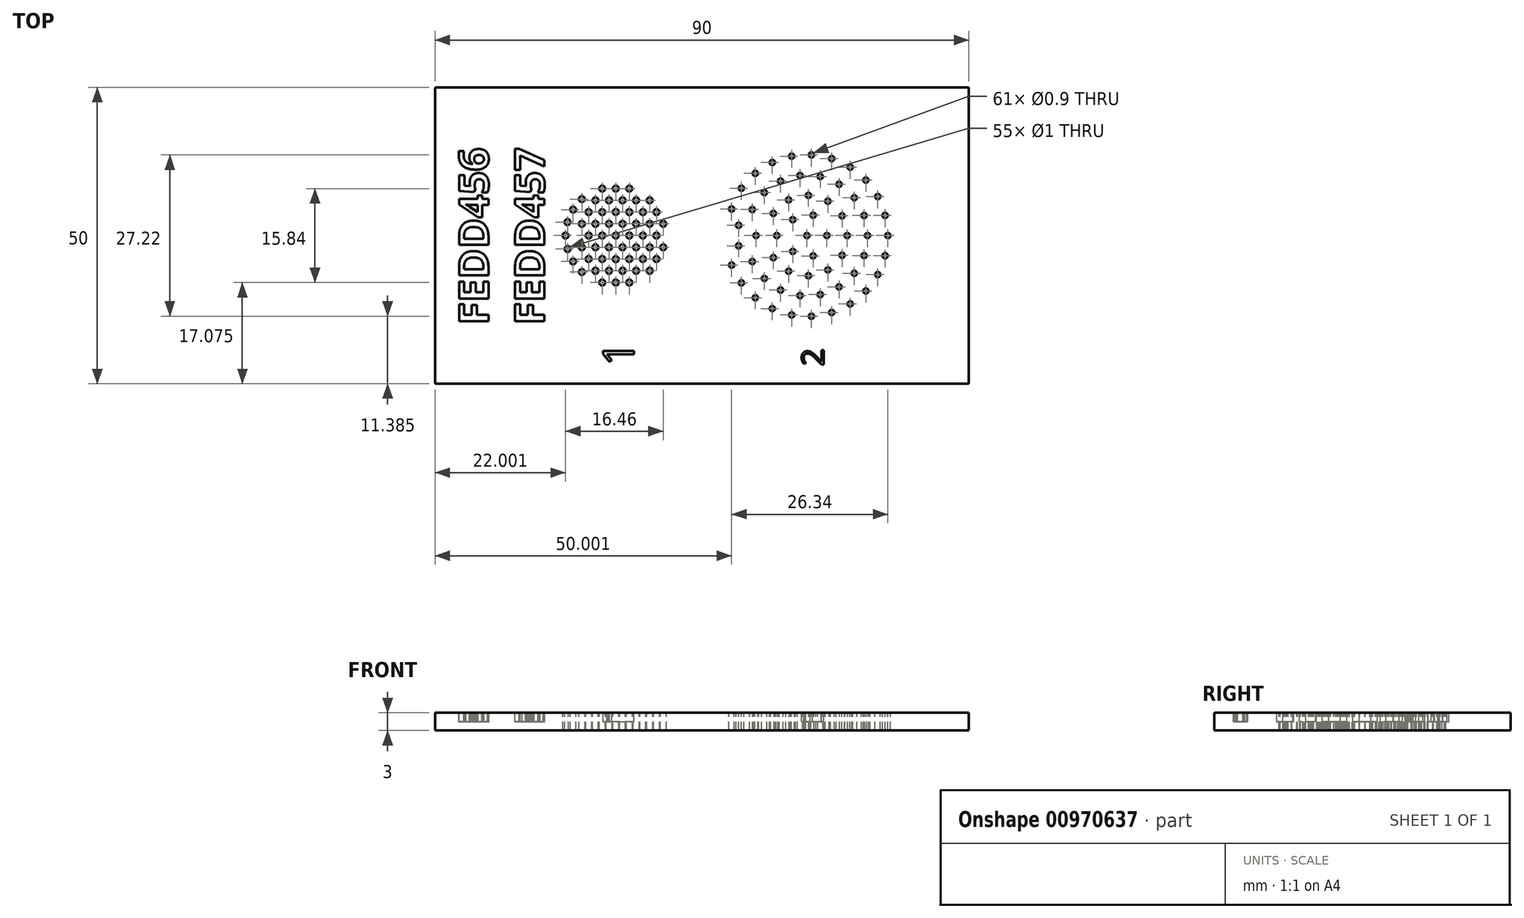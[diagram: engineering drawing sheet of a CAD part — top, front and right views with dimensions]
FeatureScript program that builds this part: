
annotation { "Feature Type Name" : "Feature", "Feature Type Description" : "" }
export const myFeature = defineFeature(function(context is Context, id is Id, definition is map)
    precondition{}
    {
        {
            var Q0;
            Q0=qCreatedBy(makeId("Top.planeOp"),FACE);
            var sketch = newSketch(context, id + "F0", { "sketchPlane" : qUnion([Q0])});
            skLineSegment(sketch, "E0.bottom", {"start": v(-43.16, 28.34) * mm, "end": v(46.84, 28.34) * mm});
            skLineSegment(sketch, "E0.top", {"start": v(-43.16, -21.66) * mm, "end": v(46.84, -21.66) * mm});
            skLineSegment(sketch, "E0.left", {"start": v(-43.16, 28.34) * mm, "end": v(-43.16, -21.66) * mm});
            skLineSegment(sketch, "E0.right", {"start": v(46.84, 28.34) * mm, "end": v(46.84, -21.66) * mm});
            skSolve(sketch);
        }
        {
            var Q0;
            Q0=makeQuery(id+"F0.imprint","IMPRINT",FACE,{"disambiguationData":[TD([[makeQuery(id+"F0.imprint","IMPRINT",EDGE,{"derivedFrom":sQuery(id+"F0.wireOp",EDGE,"E0.bottom")}),-1.0]])]});
            extrude(context, id + "F1", {"entities" : qUnion([Q0]), "depth" : 3 * mm, "offsetDistance" : 25 * mm});
        }
        {
            var Q0;
            Q0=makeQuery(id+"F1.opExtrude","CAP_FACE",FACE,{"disambiguationData":[OSD([sQuery(id+"F0.wireOp",EDGE,"E0.bottom"),sQuery(id+"F0.wireOp",EDGE,"E0.top"),sQuery(id+"F0.wireOp",EDGE,"E0.left"),sQuery(id+"F0.wireOp",EDGE,"E0.right")])],"isStart":false});
            var sketch = newSketch(context, id + "F2", { "sketchPlane" : qUnion([Q0])});
            skText(sketch, "E1", { "text": "FEDD456 \nFEDD457", "fontName": "OpenSans-Bold.ttf"});
            skText(sketch, "E2", { "text": "1", "fontName": "OpenSans-Regular.ttf"});
            skText(sketch, "E3", { "text": "2", "fontName": "OpenSans-Regular.ttf"});
            const initialGuessF2  = {"E1": [-0.03416, -0.01171, 0, 1, 0.005], "E2": [-0.00966, -0.01866, 0, 1, 0.00522], "E3": [0.02236, -0.01866, 0, 1, 0.0037]};
            skSetInitialGuess(sketch, initialGuessF2);
            skSolve(sketch);
        }
        {
            var Q0;
            Q0=qSketchRegion(id+"F2",true);
            extrude(context, id + "F3", {"entities" : qUnion([Q0]), "operationType" : NewBodyOperationType.REMOVE, "oppositeDirection" : true, "depth" : 1.5 * mm, "offsetDistance" : 25 * mm});
        }
        {
            var Q0;
            {var subQ0=sQuery(id+"F0.wireOp",EDGE,"E0.left");var subQ1=sQuery(id+"F0.wireOp",EDGE,"E0.bottom");var subQ2=sQuery(id+"F0.wireOp",EDGE,"E0.right");var subQ3=sQuery(id+"F0.wireOp",EDGE,"E0.top");Q0=makeQuery(id+"F3.boolean.opBoolean","SPLIT",FACE,{"disambiguationData":[TD([makeQuery(id+"F1.opExtrude","SWEPT_FACE",FACE,{"disambiguationData":[OSD([subQ1])]})])],"derivedFrom":makeQuery(id+"F1.opExtrude","CAP_FACE",FACE,{"disambiguationData":[OSD([subQ1,subQ3,subQ0,subQ2])],"isStart":false})});}
            var sketch = newSketch(context, id + "F4", { "sketchPlane" : qUnion([Q0])});
            skLineSegment(sketch, "E4", {"start": v(-27.8, 3.34) * mm, "end": v(2.56, 3.34) * mm});
            skLineSegment(sketch, "E5", {"start": v(-12.8, -15.66) * mm, "end": v(-12.8, 21.7) * mm});
            skCircle(sketch, "E6", {"center": v(-14.98, -4.58) * mm, "radius": 0.5 * mm});
            skCircle(sketch, "E7", {"center": v(-18.4, -2.81) * mm, "radius": 0.5 * mm});
            skCircle(sketch, "E8", {"center": v(-19.89, -1.03) * mm, "radius": 0.5 * mm});
            skCircle(sketch, "E9", {"center": v(-20.83, 1.08) * mm, "radius": 0.5 * mm});
            skCircle(sketch, "E10", {"center": v(-21.16, 3.34) * mm, "radius": 0.5 * mm});
            skCircle(sketch, "E11", {"center": v(-20.83, 5.6) * mm, "radius": 0.5 * mm});
            skCircle(sketch, "E12", {"center": v(-19.89, 7.7) * mm, "radius": 0.5 * mm});
            skCircle(sketch, "E13", {"center": v(-18.4, 9.49) * mm, "radius": 0.5 * mm});
            skCircle(sketch, "E14", {"center": v(-14.98, 11.26) * mm, "radius": 0.5 * mm});
            skCircle(sketch, "E15", {"center": v(-10.4, 11.26) * mm, "radius": 0.5 * mm});
            skCircle(sketch, "E16", {"center": v(-6.98, 9.28) * mm, "radius": 0.5 * mm});
            skCircle(sketch, "E17", {"center": v(-5.84, 7.3) * mm, "radius": 0.5 * mm});
            skCircle(sketch, "E18", {"center": v(-4.7, 5.32) * mm, "radius": 0.5 * mm});
            skCircle(sketch, "E19", {"center": v(-4.7, 1.36) * mm, "radius": 0.5 * mm});
            skCircle(sketch, "E20", {"center": v(-5.84, -0.62) * mm, "radius": 0.5 * mm});
            skCircle(sketch, "E21", {"center": v(-6.98, -2.6) * mm, "radius": 0.5 * mm});
            skCircle(sketch, "E22", {"center": v(-10.4, -4.58) * mm, "radius": 0.5 * mm});
            skCircle(sketch, "E23", {"center": v(-12.7, -4.58) * mm, "radius": 0.5 * mm});
            skCircle(sketch, "E24", {"center": v(-18.4, 5.32) * mm, "radius": 0.5 * mm});
            skCircle(sketch, "E25", {"center": v(-17.27, 7.3) * mm, "radius": 0.5 * mm});
            skCircle(sketch, "E26", {"center": v(-16.13, 9.28) * mm, "radius": 0.5 * mm});
            skCircle(sketch, "E27", {"center": v(-13.84, 9.28) * mm, "radius": 0.5 * mm});
            skCircle(sketch, "E28", {"center": v(-16.13, 5.32) * mm, "radius": 0.5 * mm});
            skCircle(sketch, "E29", {"center": v(-14.98, 7.3) * mm, "radius": 0.5 * mm});
            skCircle(sketch, "E30", {"center": v(-13.84, 5.32) * mm, "radius": 0.5 * mm});
            skCircle(sketch, "E31", {"center": v(-12.7, 11.26) * mm, "radius": 0.5 * mm});
            skCircle(sketch, "E32", {"center": v(-9.27, 9.28) * mm, "radius": 0.5 * mm});
            skCircle(sketch, "E33", {"center": v(-8.13, 7.3) * mm, "radius": 0.5 * mm});
            skCircle(sketch, "E34", {"center": v(-9.27, 5.32) * mm, "radius": 0.5 * mm});
            skCircle(sketch, "E35", {"center": v(-10.4, 7.3) * mm, "radius": 0.5 * mm});
            skCircle(sketch, "E36", {"center": v(-11.56, 5.32) * mm, "radius": 0.5 * mm});
            skCircle(sketch, "E37", {"center": v(-12.7, 7.32) * mm, "radius": 0.5 * mm});
            skCircle(sketch, "E38", {"center": v(-17.27, 3.34) * mm, "radius": 0.5 * mm});
            skCircle(sketch, "E39", {"center": v(-14.98, 3.34) * mm, "radius": 0.5 * mm});
            skCircle(sketch, "E40", {"center": v(-12.7, 3.34) * mm, "radius": 0.5 * mm});
            skCircle(sketch, "E41", {"center": v(-10.4, 3.34) * mm, "radius": 0.5 * mm});
            skCircle(sketch, "E42", {"center": v(-8.13, 3.34) * mm, "radius": 0.5 * mm});
            skCircle(sketch, "E43", {"center": v(-5.84, 3.34) * mm, "radius": 0.5 * mm});
            skCircle(sketch, "E44", {"center": v(-18.4, 1.36) * mm, "radius": 0.5 * mm});
            skCircle(sketch, "E45", {"center": v(-16.13, 1.36) * mm, "radius": 0.5 * mm});
            skCircle(sketch, "E46", {"center": v(-13.84, 1.36) * mm, "radius": 0.5 * mm});
            skCircle(sketch, "E47", {"center": v(-11.56, 1.36) * mm, "radius": 0.5 * mm});
            skCircle(sketch, "E48", {"center": v(-9.27, 1.36) * mm, "radius": 0.5 * mm});
            skCircle(sketch, "E49", {"center": v(-6.98, 1.36) * mm, "radius": 0.5 * mm});
            skCircle(sketch, "E50", {"center": v(-17.27, -0.62) * mm, "radius": 0.5 * mm});
            skCircle(sketch, "E51", {"center": v(-14.98, -0.62) * mm, "radius": 0.5 * mm});
            skCircle(sketch, "E52", {"center": v(-12.7, -0.64) * mm, "radius": 0.5 * mm});
            skCircle(sketch, "E53", {"center": v(-10.4, -0.62) * mm, "radius": 0.5 * mm});
            skCircle(sketch, "E54", {"center": v(-8.13, -0.62) * mm, "radius": 0.5 * mm});
            skCircle(sketch, "E55", {"center": v(-16.13, -2.6) * mm, "radius": 0.5 * mm});
            skCircle(sketch, "E56", {"center": v(-13.84, -2.6) * mm, "radius": 0.5 * mm});
            skCircle(sketch, "E57", {"center": v(-11.56, -2.6) * mm, "radius": 0.5 * mm});
            skCircle(sketch, "E58", {"center": v(-9.27, -2.6) * mm, "radius": 0.5 * mm});
            skCircle(sketch, "E59", {"center": v(-6.98, 5.32) * mm, "radius": 0.5 * mm});
            skCircle(sketch, "E60", {"center": v(-11.56, 9.28) * mm, "radius": 0.5 * mm});
            skLineSegment(sketch, "E61", {"start": v(4.04, 3.34) * mm, "end": v(37.05, 3.34) * mm});
            skLineSegment(sketch, "E62", {"start": v(19.54, -13.72) * mm, "end": v(19.54, 21.34) * mm});
            skCircle(sketch, "E63", {"center": v(6.84, 7.82) * mm, "radius": 0.45 * mm});
            skCircle(sketch, "E64", {"center": v(8.5, 11.32) * mm, "radius": 0.45 * mm});
            skCircle(sketch, "E65", {"center": v(10.83, 13.83) * mm, "radius": 0.45 * mm});
            skCircle(sketch, "E66", {"center": v(13.7, 15.66) * mm, "radius": 0.45 * mm});
            skCircle(sketch, "E67", {"center": v(16.97, 16.73) * mm, "radius": 0.45 * mm});
            skCircle(sketch, "E68", {"center": v(20.3, 16.95) * mm, "radius": 0.45 * mm});
            skCircle(sketch, "E69", {"center": v(23.71, 16.32) * mm, "radius": 0.45 * mm});
            skCircle(sketch, "E70", {"center": v(26.83, 14.87) * mm, "radius": 0.45 * mm});
            skCircle(sketch, "E71", {"center": v(29.47, 12.69) * mm, "radius": 0.45 * mm});
            skCircle(sketch, "E72", {"center": v(31.48, 9.92) * mm, "radius": 0.45 * mm});
            skCircle(sketch, "E73", {"center": v(32.72, 6.74) * mm, "radius": 0.45 * mm});
            skCircle(sketch, "E74", {"center": v(32.72, -0.06) * mm, "radius": 0.45 * mm});
            skCircle(sketch, "E75", {"center": v(31.48, -3.24) * mm, "radius": 0.45 * mm});
            skCircle(sketch, "E76", {"center": v(29.47, -6.01) * mm, "radius": 0.45 * mm});
            skCircle(sketch, "E77", {"center": v(26.83, -8.2) * mm, "radius": 0.45 * mm});
            skCircle(sketch, "E78", {"center": v(23.71, -9.64) * mm, "radius": 0.45 * mm});
            skCircle(sketch, "E79", {"center": v(20.3, -10.27) * mm, "radius": 0.45 * mm});
            skCircle(sketch, "E80", {"center": v(16.97, -10.05) * mm, "radius": 0.45 * mm});
            skCircle(sketch, "E81", {"center": v(13.7, -8.98) * mm, "radius": 0.45 * mm});
            skCircle(sketch, "E82", {"center": v(10.83, -7.15) * mm, "radius": 0.45 * mm});
            skCircle(sketch, "E83", {"center": v(8.5, -4.64) * mm, "radius": 0.45 * mm});
            skCircle(sketch, "E84", {"center": v(6.84, -1.64) * mm, "radius": 0.45 * mm});
            skCircle(sketch, "E85", {"center": v(8.01, 5.07) * mm, "radius": 0.45 * mm});
            skCircle(sketch, "E86", {"center": v(10.32, 7.73) * mm, "radius": 0.45 * mm});
            skCircle(sketch, "E87", {"center": v(12.35, 10.58) * mm, "radius": 0.45 * mm});
            skCircle(sketch, "E88", {"center": v(15.1, 12.53) * mm, "radius": 0.45 * mm});
            skCircle(sketch, "E89", {"center": v(18.37, 13.47) * mm, "radius": 0.45 * mm});
            skCircle(sketch, "E90", {"center": v(21.78, 13.3) * mm, "radius": 0.45 * mm});
            skCircle(sketch, "E91", {"center": v(24.95, 12) * mm, "radius": 0.45 * mm});
            skCircle(sketch, "E92", {"center": v(27.52, 9.72) * mm, "radius": 0.45 * mm});
            skCircle(sketch, "E93", {"center": v(19.8, 10.12) * mm, "radius": 0.45 * mm});
            skCircle(sketch, "E94", {"center": v(23.07, 9.13) * mm, "radius": 0.45 * mm});
            skCircle(sketch, "E95", {"center": v(25.46, 6.67) * mm, "radius": 0.45 * mm});
            skCircle(sketch, "E96", {"center": v(20.58, 6.77) * mm, "radius": 0.45 * mm});
            skCircle(sketch, "E97", {"center": v(13.88, 7.07) * mm, "radius": 0.45 * mm});
            skCircle(sketch, "E98", {"center": v(16.44, 9.36) * mm, "radius": 0.45 * mm});
            skCircle(sketch, "E99", {"center": v(17.15, 6) * mm, "radius": 0.45 * mm});
            skCircle(sketch, "E100", {"center": v(8.01, 1.6) * mm, "radius": 0.45 * mm});
            skCircle(sketch, "E101", {"center": v(10.32, -1.05) * mm, "radius": 0.45 * mm});
            skCircle(sketch, "E102", {"center": v(12.35, -3.9) * mm, "radius": 0.45 * mm});
            skCircle(sketch, "E103", {"center": v(15.1, -5.85) * mm, "radius": 0.45 * mm});
            skCircle(sketch, "E104", {"center": v(18.37, -6.8) * mm, "radius": 0.45 * mm});
            skCircle(sketch, "E105", {"center": v(13.88, -0.4) * mm, "radius": 0.45 * mm});
            skCircle(sketch, "E106", {"center": v(16.44, -2.68) * mm, "radius": 0.45 * mm});
            skCircle(sketch, "E107", {"center": v(17.15, 0.67) * mm, "radius": 0.45 * mm});
            skCircle(sketch, "E108", {"center": v(29.75, 3.34) * mm, "radius": 0.45 * mm});
            skCircle(sketch, "E109", {"center": v(25.46, 0) * mm, "radius": 0.45 * mm});
            skCircle(sketch, "E110", {"center": v(29.17, -0.04) * mm, "radius": 0.45 * mm});
            skCircle(sketch, "E111", {"center": v(27.52, -3.04) * mm, "radius": 0.45 * mm});
            skCircle(sketch, "E112", {"center": v(24.95, -5.31) * mm, "radius": 0.45 * mm});
            skCircle(sketch, "E113", {"center": v(21.78, -6.62) * mm, "radius": 0.45 * mm});
            skCircle(sketch, "E114", {"center": v(19.8, -3.44) * mm, "radius": 0.45 * mm});
            skCircle(sketch, "E115", {"center": v(20.58, -0.1) * mm, "radius": 0.45 * mm});
            skCircle(sketch, "E116", {"center": v(19.54, 3.34) * mm, "radius": 0.45 * mm});
            skCircle(sketch, "E117", {"center": v(10.95, 3.34) * mm, "radius": 0.45 * mm});
            skCircle(sketch, "E118", {"center": v(14.46, 3.34) * mm, "radius": 0.45 * mm});
            skCircle(sketch, "E119", {"center": v(22.9, 3.34) * mm, "radius": 0.45 * mm});
            skCircle(sketch, "E120", {"center": v(26.32, 3.34) * mm, "radius": 0.45 * mm});
            skCircle(sketch, "E121", {"center": v(33.18, 3.34) * mm, "radius": 0.45 * mm});
            skCircle(sketch, "E122", {"center": v(29.17, 6.72) * mm, "radius": 0.45 * mm});
            skCircle(sketch, "E123", {"center": v(23.07, -2.45) * mm, "radius": 0.45 * mm});
            skSolve(sketch);
        }
        {
            var Q0;
            Q0 = qSketchRegion(id + "F4", true);
            extrude(context, id + "F5", {"entities" : qUnion([Q0]), "operationType" : NewBodyOperationType.REMOVE, "endBound" : BoundingType.UP_TO_NEXT, "oppositeDirection" : true, "depth" : 25 * mm, "offsetDistance" : 25 * mm});
        }
    });
